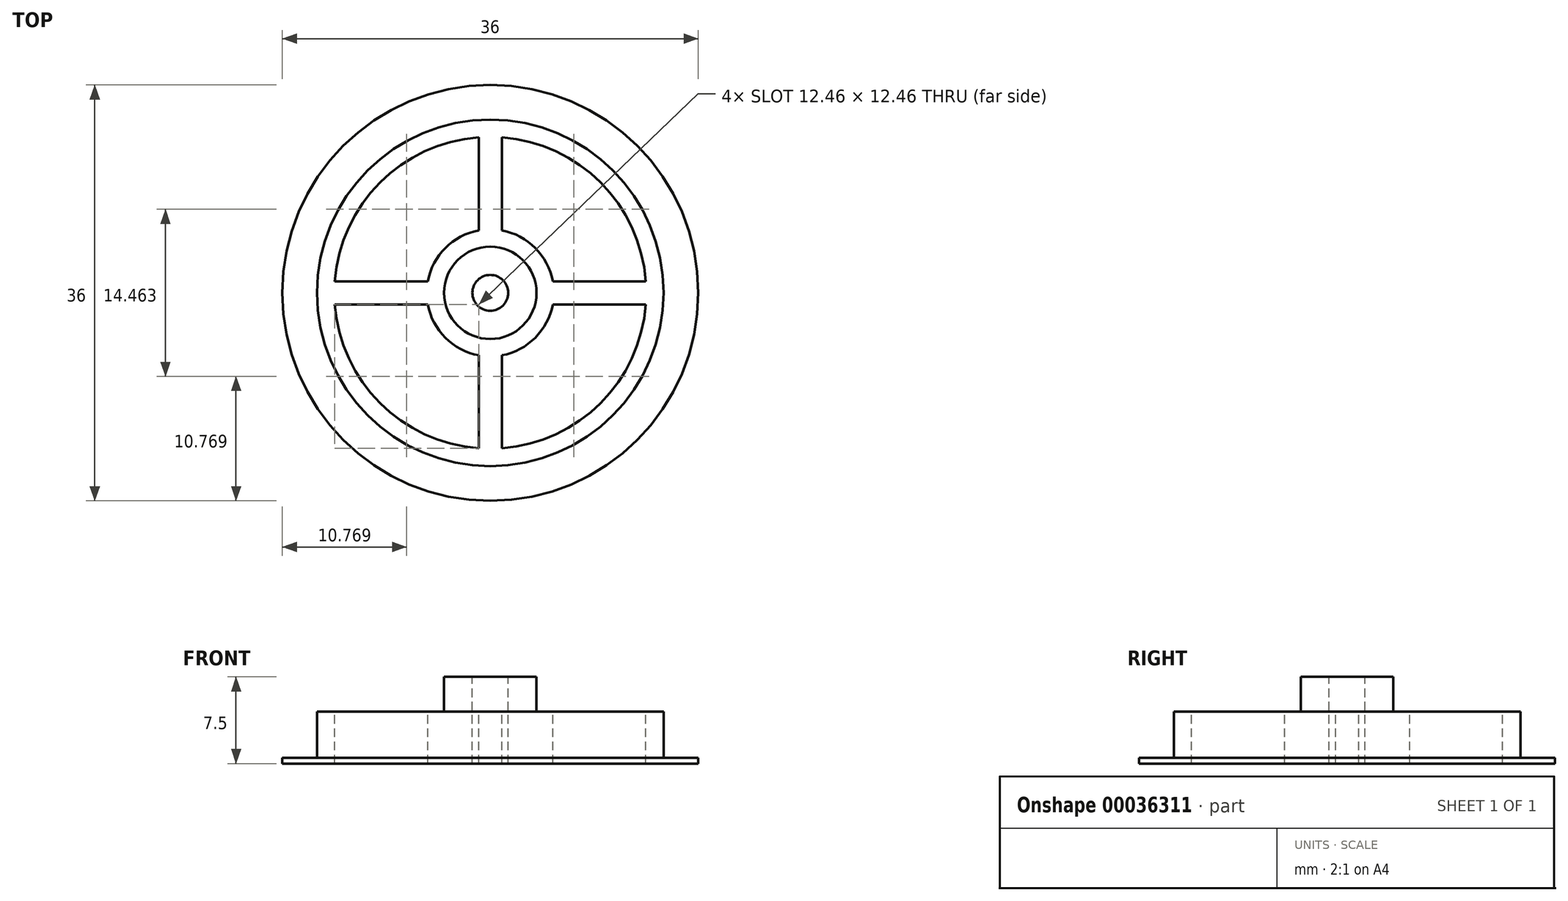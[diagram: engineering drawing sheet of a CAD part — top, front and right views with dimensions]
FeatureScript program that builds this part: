
annotation { "Feature Type Name" : "Feature", "Feature Type Description" : "" }
export const myFeature = defineFeature(function(context is Context, id is Id, definition is map)
    precondition{}
    {
        {
            var Q0;
            Q0=qCreatedBy(makeId("Top.planeOp"),FACE);
            var sketch = newSketch(context, id + "F0", { "sketchPlane" : qUnion([Q0])});
            skCircle(sketch, "E0", {"center": v(0, 0) * mm, "radius": 15 * mm});
            skSolve(sketch);
        }
        {
            var Q0;
            Q0=makeQuery(id+"F0.imprint","IMPRINT",FACE,{"disambiguationData":[TD([[makeQuery(id+"F0.imprint","IMPRINT",EDGE,{"derivedFrom":sQuery(id+"F0.wireOp",EDGE,"E0")}),1.0]])]});
            extrude(context, id + "F1", {"entities" : qUnion([Q0]), "depth" : 4 * mm});
        }
        {
            var Q0;
            Q0=makeQuery(id+"F1.opExtrude","CAP_FACE",FACE,{"disambiguationData":[OSD([sQuery(id+"F0.wireOp",EDGE,"E0")])],"isStart":true});
            var sketch = newSketch(context, id + "F2", { "sketchPlane" : qUnion([Q0])});
            skCircle(sketch, "E1", {"center": v(0, 0) * mm, "radius": 18 * mm});
            skSolve(sketch);
        }
        {
            var Q0;
            Q0=makeQuery(id+"F2.imprint","IMPRINT",FACE,{"disambiguationData":[TD([[makeQuery(id+"F2.imprint","IMPRINT",EDGE,{"derivedFrom":makeQuery(id+"F1.opExtrude","CAP_EDGE",EDGE,{"disambiguationData":[OSD([sQuery(id+"F0.wireOp",EDGE,"E0")])],"isStart":true})}),-1.0]])]});
            var Q1;
            Q1=makeQuery(id+"F2.imprint","IMPRINT",FACE,{"disambiguationData":[TD([[makeQuery(id+"F2.imprint","IMPRINT",EDGE,{"derivedFrom":sQuery(id+"F2.wireOp",EDGE,"E1")}),1.0]])]});
            extrude(context, id + "F3", {"entities" : qUnion([Q0, Q1]), "operationType" : NewBodyOperationType.ADD, "depth" : 0.5 * mm});
        }
        {
            var Q0;
            Q0=makeQuery(id+"F1.opExtrude","CAP_FACE",FACE,{"disambiguationData":[OSD([sQuery(id+"F0.wireOp",EDGE,"E0")])],"isStart":false});
            var sketch = newSketch(context, id + "F4", { "sketchPlane" : qUnion([Q0])});
            skCircle(sketch, "E2", {"center": v(0, 0) * mm, "radius": 4 * mm});
            skSolve(sketch);
        }
        {
            var Q0;
            Q0=makeQuery(id+"F4.imprint","IMPRINT",FACE,{"disambiguationData":[TD([[makeQuery(id+"F4.imprint","IMPRINT",EDGE,{"derivedFrom":sQuery(id+"F4.wireOp",EDGE,"E2")}),1.0]])]});
            extrude(context, id + "F5", {"entities" : qUnion([Q0]), "operationType" : NewBodyOperationType.ADD, "depth" : 3 * mm});
        }
        {
            var Q0;
            Q0=makeQuery(id+"F5.opExtrude","CAP_FACE",FACE,{"disambiguationData":[OSD([sQuery(id+"F4.wireOp",EDGE,"E2")])],"isStart":false});
            var sketch = newSketch(context, id + "F6", { "sketchPlane" : qUnion([Q0])});
            skCircle(sketch, "E3", {"center": v(0, 0) * mm, "radius": 1.55 * mm});
            skSolve(sketch);
        }
        {
            var Q0;
            Q0=makeQuery(id+"F6.imprint","IMPRINT",FACE,{"disambiguationData":[TD([[makeQuery(id+"F6.imprint","IMPRINT",EDGE,{"derivedFrom":sQuery(id+"F6.wireOp",EDGE,"E3")}),1.0]])]});
            extrude(context, id + "F7", {"entities" : qUnion([Q0]), "operationType" : NewBodyOperationType.REMOVE, "endBound" : BoundingType.UP_TO_NEXT, "oppositeDirection" : true, "depth" : 25 * mm});
        }
        {
            var Q0;
            Q0=makeQuery(id+"F1.opExtrude","CAP_FACE",FACE,{"disambiguationData":[OSD([sQuery(id+"F0.wireOp",EDGE,"E0")])],"isStart":false});
            var sketch = newSketch(context, id + "F8", { "sketchPlane" : qUnion([Q0])});
            skCircle(sketch, "E4", {"center": v(0, 0) * mm, "radius": 5.5 * mm});
            skLineSegment(sketch, "E5.left", {"start": v(-1, 14.97) * mm, "end": v(-1, 5.4) * mm});
            skLineSegment(sketch, "E5.right", {"start": v(1, 14.97) * mm, "end": v(1, 5.4) * mm});
            skLineSegment(sketch, "E6", {"start": v(0, 15) * mm, "end": v(0, 5.5) * mm, "construction": true});
            skLineSegment(sketch, "E7", {"start": v(1, -5.4) * mm, "end": v(1, -14.97) * mm});
            skLineSegment(sketch, "E8", {"start": v(-1, -5.4) * mm, "end": v(-1, -14.97) * mm});
            skLineSegment(sketch, "E9", {"start": v(0, 0) * mm, "end": v(15, 0) * mm, "construction": true});
            skLineSegment(sketch, "E10.0", {"start": v(3.87, 1) * mm, "end": v(14.97, 1) * mm});
            skLineSegment(sketch, "E11.0", {"start": v(3.87, -1) * mm, "end": v(14.97, -1) * mm});
            skLineSegment(sketch, "E12", {"start": v(-3.87, -1) * mm, "end": v(-14.97, -1) * mm});
            skLineSegment(sketch, "E13", {"start": v(-5.4, 1) * mm, "end": v(-14.97, 1) * mm});
            skCircle(sketch, "E14", {"center": v(0, 0) * mm, "radius": 13.5 * mm});
            skSolve(sketch);
        }
        {
            var Q0;
            {var subQ3=sQuery(id+"F8.wireOp",EDGE,"E5.left");var subQ5=sQuery(id+"F8.wireOp",EDGE,"E4");var subQ7=makeQuery(id+"F8.imprint","INTERSECT",VERTEX,{"derivedFrom":[subQ5,subQ3]});Q0=makeQuery(id+"F8.imprint","IMPRINT",FACE,{"disambiguationData":[TD([[makeQuery(id+"F8.imprint","IMPRINT",EDGE,{"disambiguationData":[TD([[subQ7,-1.0]])],"derivedFrom":subQ5}),-1.0]])]});}
            var Q1;
            {var subQ3=sQuery(id+"F8.wireOp",EDGE,"E5.right");var subQ5=sQuery(id+"F8.wireOp",EDGE,"E4");var subQ7=makeQuery(id+"F8.imprint","INTERSECT",VERTEX,{"derivedFrom":[subQ5,subQ3]});Q1=makeQuery(id+"F8.imprint","IMPRINT",FACE,{"disambiguationData":[TD([[makeQuery(id+"F8.imprint","IMPRINT",EDGE,{"disambiguationData":[TD([[subQ7,1.0]])],"derivedFrom":subQ5}),-1.0]])]});}
            var Q2;
            {var subQ3=sQuery(id+"F8.wireOp",EDGE,"E7");var subQ5=sQuery(id+"F8.wireOp",EDGE,"E4");var subQ7=makeQuery(id+"F8.imprint","INTERSECT",VERTEX,{"derivedFrom":[subQ5,subQ3]});Q2=makeQuery(id+"F8.imprint","IMPRINT",FACE,{"disambiguationData":[TD([[makeQuery(id+"F8.imprint","IMPRINT",EDGE,{"disambiguationData":[TD([[subQ7,-1.0]])],"derivedFrom":subQ5}),-1.0]])]});}
            var Q3;
            {var subQ3=sQuery(id+"F8.wireOp",EDGE,"E8");var subQ5=sQuery(id+"F8.wireOp",EDGE,"E4");var subQ7=makeQuery(id+"F8.imprint","INTERSECT",VERTEX,{"derivedFrom":[subQ5,subQ3]});Q3=makeQuery(id+"F8.imprint","IMPRINT",FACE,{"disambiguationData":[TD([[makeQuery(id+"F8.imprint","IMPRINT",EDGE,{"disambiguationData":[TD([[subQ7,1.0]])],"derivedFrom":subQ5}),-1.0]])]});}
            extrude(context, id + "F9", {"entities" : qUnion([Q0, Q1, Q2, Q3]), "operationType" : NewBodyOperationType.REMOVE, "endBound" : BoundingType.UP_TO_NEXT, "oppositeDirection" : true, "depth" : 25 * mm});
        }
    });
